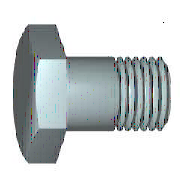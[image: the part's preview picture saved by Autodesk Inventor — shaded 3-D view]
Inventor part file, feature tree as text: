
AUTODESK INVENTOR PART (.ipt)
format: ipt  version: 2025 (Build 290162000, 162)  size: 196,096 bytes
history: native  units: mm (DEFAULTED — no unit token found)
features: other x1, extrude x1, chamfer x1, plane x1
ambient origin geometry x7: Origin, YZ Plane, XZ Plane, X Axis, Y Axis, Z Axis, Center Point
bodies: Solid1 (feature_tree)
feature tree (4):
  other  "轴承体"
  extrude  "头"  Depth=35.0mm
  chamfer  "倒角1"  Distance=26.0mm
  plane  "Work Plane1"
